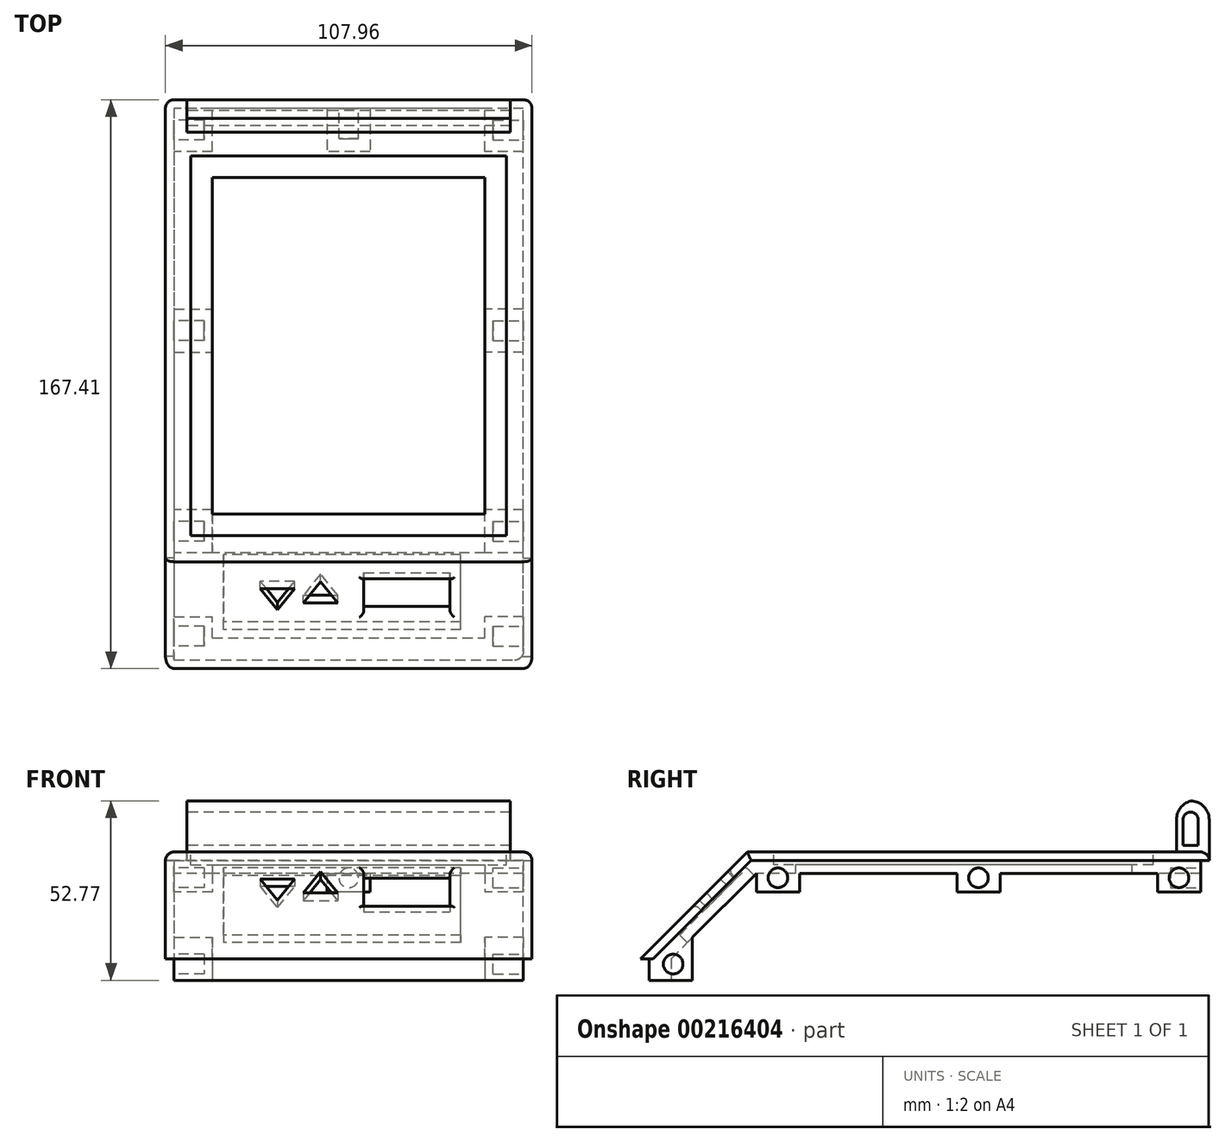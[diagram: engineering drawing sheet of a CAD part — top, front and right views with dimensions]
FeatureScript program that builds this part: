
annotation { "Feature Type Name" : "Feature", "Feature Type Description" : "" }
export const myFeature = defineFeature(function(context is Context, id is Id, definition is map)
    precondition{}
    {
        {
            var Q0;
            Q0=qCreatedBy(makeId("Top.planeOp"),FACE);
            var sketch = newSketch(context, id + "F0", { "sketchPlane" : qUnion([Q0])});
            skLineSegment(sketch, "E0.bottom", {"start": v(-40.13, 49.53) * mm, "end": v(40.13, 49.53) * mm});
            skLineSegment(sketch, "E0.top", {"start": v(-40.13, -49.53) * mm, "end": v(40.13, -49.53) * mm});
            skLineSegment(sketch, "E0.left", {"start": v(-40.13, 49.53) * mm, "end": v(-40.13, -49.53) * mm});
            skLineSegment(sketch, "E0.right", {"start": v(40.13, 49.53) * mm, "end": v(40.13, -49.53) * mm});
            skPoint(sketch, "E0.middle", {"position": v(0, 0) * mm});
            skLineSegment(sketch, "E1.bottom", {"start": v(53.97, -60.96) * mm, "end": v(-53.98, -60.96) * mm});
            skLineSegment(sketch, "E1.top", {"start": v(53.97, 72.4) * mm, "end": v(-53.98, 72.39) * mm});
            skLineSegment(sketch, "E1.left", {"start": v(53.98, -60.96) * mm, "end": v(53.98, 72.4) * mm});
            skLineSegment(sketch, "E1.right", {"start": v(-53.98, -60.96) * mm, "end": v(-53.98, 72.39) * mm});
            skSolve(sketch);
        }
        {
            var Q0;
            Q0 = qSketchRegion(id + "F0", true);
            extrude(context, id + "F1", {"entities" : qUnion([Q0]), "depth" : 6.35 * mm});
        }
        {
            var Q0;
            Q0=makeQuery(id+"F1.opExtrude","CAP_FACE",FACE,{"disambiguationData":[OSD([sQuery(id+"F0.wireOp",EDGE,"E0.bottom"),sQuery(id+"F0.wireOp",EDGE,"E0.top"),sQuery(id+"F0.wireOp",EDGE,"E0.left"),sQuery(id+"F0.wireOp",EDGE,"E0.right"),sQuery(id+"F0.wireOp",EDGE,"E1.bottom"),sQuery(id+"F0.wireOp",EDGE,"E1.top"),sQuery(id+"F0.wireOp",EDGE,"E1.left"),sQuery(id+"F0.wireOp",EDGE,"E1.right")])],"isStart":false});
            var sketch = newSketch(context, id + "F2", { "sketchPlane" : qUnion([Q0])});
            skPoint(sketch, "E2.middle", {"position": v(0, 0) * mm});
            skLineSegment(sketch, "E3.0", {"start": v(-46.48, 55.88) * mm, "end": v(46.48, 55.88) * mm});
            skLineSegment(sketch, "E3.1", {"start": v(-46.48, 55.88) * mm, "end": v(-46.48, -55.88) * mm});
            skLineSegment(sketch, "E3.2", {"start": v(-46.48, -55.88) * mm, "end": v(46.48, -55.88) * mm});
            skLineSegment(sketch, "E3.3", {"start": v(46.48, 55.88) * mm, "end": v(46.48, -55.88) * mm});
            skSolve(sketch);
        }
        {
            var Q0;
            Q0 = qSketchRegion(id + "F2", true);
            extrude(context, id + "F3", {"entities" : qUnion([Q0]), "operationType" : NewBodyOperationType.REMOVE, "oppositeDirection" : true, "depth" : 3.8 * mm});
        }
        {
            var Q0;
            Q0=makeQuery(id+"F1.opExtrude","SWEPT_FACE",FACE,{"disambiguationData":[OSD([sQuery(id+"F0.wireOp",EDGE,"E1.left")])]});
            var sketch = newSketch(context, id + "F4", { "sketchPlane" : qUnion([Q0])});
            skLineSegment(sketch, "E4", {"start": v(-60.96, 0) * mm, "end": v(-86.04, -25.08) * mm});
            skLineSegment(sketch, "E5", {"start": v(-95.02, -25.08) * mm, "end": v(-63.6, 6.35) * mm});
            skLineSegment(sketch, "E6", {"start": v(-63.6, 6.35) * mm, "end": v(-60.96, 6.35) * mm});
            skLineSegment(sketch, "E7", {"start": v(-60.96, 0) * mm, "end": v(-60.96, 6.35) * mm});
            skLineSegment(sketch, "E8", {"start": v(-95.02, -25.08) * mm, "end": v(-95.02, -31.43) * mm});
            skLineSegment(sketch, "E9", {"start": v(-86.04, -31.43) * mm, "end": v(-86.04, -25.08) * mm});
            skLineSegment(sketch, "E10", {"start": v(-86.04, -25.08) * mm, "end": v(-95.02, -25.08) * mm});
            skLineSegment(sketch, "E11", {"start": v(-95.02, -31.43) * mm, "end": v(-86.04, -31.43) * mm});
            skSolve(sketch);
        }
        {
            var Q0;
            Q0 = qSketchRegion(id + "F4", true);
            var Q1;
            Q1=makeQuery(id+"F1.opExtrude","SWEPT_FACE",FACE,{"disambiguationData":[OSD([sQuery(id+"F0.wireOp",EDGE,"E1.right")])]});
            extrude(context, id + "F5", {"entities" : qUnion([Q0]), "operationType" : NewBodyOperationType.ADD, "endBound" : BoundingType.UP_TO_SURFACE, "oppositeDirection" : true, "endBoundEntityFace" : qUnion([Q1]), "depth" : 101.6 * mm});
        }
        {
            var Q0;
            Q0=makeQuery(id+"F5.opExtrude","SWEPT_FACE",FACE,{"disambiguationData":[OSD([sQuery(id+"F4.wireOp",EDGE,"E8")])]});
            var sketch = newSketch(context, id + "F6", { "sketchPlane" : qUnion([Q0])});
            skLineSegment(sketch, "E12.bottom", {"start": v(53.98, -25.08) * mm, "end": v(-53.97, -25.08) * mm});
            skLineSegment(sketch, "E12.top", {"start": v(53.98, -31.43) * mm, "end": v(-53.97, -31.43) * mm});
            skLineSegment(sketch, "E12.left", {"start": v(53.98, -25.08) * mm, "end": v(53.98, -31.43) * mm});
            skLineSegment(sketch, "E12.right", {"start": v(-53.97, -25.08) * mm, "end": v(-53.97, -31.43) * mm});
            skSolve(sketch);
        }
        {
            var Q0;
            Q0 = qSketchRegion(id + "F6", true);
            extrude(context, id + "F7", {"entities" : qUnion([Q0]), "operationType" : NewBodyOperationType.REMOVE, "oppositeDirection" : true, "depth" : 2.54 * mm});
        }
        {
            var Q0;
            Q0=makeQuery(id+"F5.boolean.opBoolean","MERGE",FACE,{"derivedFrom":[makeQuery(id+"F1.opExtrude","SWEPT_FACE",FACE,{"disambiguationData":[OSD([sQuery(id+"F0.wireOp",EDGE,"E1.left")])]}),makeQuery(id+"F5.opExtrude","CAP_FACE",FACE,{"disambiguationData":[OSD([sQuery(id+"F4.wireOp",EDGE,"E4"),sQuery(id+"F4.wireOp",EDGE,"E5"),sQuery(id+"F4.wireOp",EDGE,"E6"),sQuery(id+"F4.wireOp",EDGE,"E7"),sQuery(id+"F4.wireOp",EDGE,"E8"),sQuery(id+"F4.wireOp",EDGE,"E9"),sQuery(id+"F4.wireOp",EDGE,"E11")])],"isStart":true})]});
            var sketch = newSketch(context, id + "F8", { "sketchPlane" : qUnion([Q0])});
            skLineSegment(sketch, "E13.0", {"start": v(-62.54, 3.81) * mm, "end": v(72.4, 3.81) * mm});
            skLineSegment(sketch, "E13.1", {"start": v(-103.18, -36.83) * mm, "end": v(-62.54, 3.81) * mm});
            skLineSegment(sketch, "E14", {"start": v(72.4, 3.81) * mm, "end": v(72.4, -36.83) * mm});
            skLineSegment(sketch, "E15", {"start": v(72.4, -36.83) * mm, "end": v(-103.18, -36.83) * mm});
            skLineSegment(sketch, "E16", {"start": v(-92.48, -25.08) * mm, "end": v(-91.43, -25.08) * mm});
            skLineSegment(sketch, "E17", {"start": v(-91.43, -25.08) * mm, "end": v(-92.48, -26.13) * mm});
            skLineSegment(sketch, "E18", {"start": v(-92.48, -26.13) * mm, "end": v(-92.48, -25.08) * mm});
            skSolve(sketch);
        }
        {
            var Q0;
            Q0 = qSketchRegion(id + "F8", true);
            extrude(context, id + "F9", {"entities" : qUnion([Q0]), "operationType" : NewBodyOperationType.REMOVE, "oppositeDirection" : true, "depth" : 2.54 * mm});
        }
        {
            var Q0;
            Q0=makeQuery(id+"F1.opExtrude","SWEPT_FACE",FACE,{"disambiguationData":[OSD([sQuery(id+"F0.wireOp",EDGE,"E1.top")])]});
            var sketch = newSketch(context, id + "F10", { "sketchPlane" : qUnion([Q0])});
            skLineSegment(sketch, "E19.bottom", {"start": v(-51.43, 3.81) * mm, "end": v(53.98, 3.81) * mm});
            skLineSegment(sketch, "E19.top", {"start": v(-51.43, 0) * mm, "end": v(53.98, 0) * mm});
            skLineSegment(sketch, "E19.left", {"start": v(-51.43, 3.81) * mm, "end": v(-51.43, 0) * mm});
            skLineSegment(sketch, "E19.right", {"start": v(53.98, 3.81) * mm, "end": v(53.98, 0) * mm});
            skSolve(sketch);
        }
        {
            var Q0;
            Q0 = qSketchRegion(id + "F10", true);
            extrude(context, id + "F11", {"entities" : qUnion([Q0]), "operationType" : NewBodyOperationType.REMOVE, "oppositeDirection" : true, "depth" : 2.54 * mm});
        }
        {
            var Q0;
            Q0=makeQuery(id+"F5.boolean.opBoolean","MERGE",FACE,{"derivedFrom":[makeQuery(id+"F1.opExtrude","SWEPT_FACE",FACE,{"disambiguationData":[OSD([sQuery(id+"F0.wireOp",EDGE,"E1.right")])]}),makeQuery(id+"F5.opExtrude","CAP_FACE",FACE,{"disambiguationData":[OSD([sQuery(id+"F4.wireOp",EDGE,"E4"),sQuery(id+"F4.wireOp",EDGE,"E5"),sQuery(id+"F4.wireOp",EDGE,"E6"),sQuery(id+"F4.wireOp",EDGE,"E7"),sQuery(id+"F4.wireOp",EDGE,"E8"),sQuery(id+"F4.wireOp",EDGE,"E9"),sQuery(id+"F4.wireOp",EDGE,"E11")])],"isStart":false})]});
            var sketch = newSketch(context, id + "F12", { "sketchPlane" : qUnion([Q0])});
            skLineSegment(sketch, "E20", {"start": v(-69.85, 3.81) * mm, "end": v(62.54, 3.81) * mm});
            skLineSegment(sketch, "E21", {"start": v(62.54, 3.81) * mm, "end": v(91.43, -25.08) * mm});
            skLineSegment(sketch, "E22", {"start": v(91.43, -25.08) * mm, "end": v(92.48, -25.08) * mm});
            skLineSegment(sketch, "E23", {"start": v(92.48, -25.08) * mm, "end": v(92.48, -36.69) * mm});
            skLineSegment(sketch, "E24", {"start": v(92.48, -36.69) * mm, "end": v(-69.85, -36.69) * mm});
            skLineSegment(sketch, "E25", {"start": v(-69.85, -36.69) * mm, "end": v(-69.85, 3.81) * mm});
            skLineSegment(sketch, "E26", {"start": v(92.48, -25.08) * mm, "end": v(91.43, -25.08) * mm});
            skSolve(sketch);
        }
        {
            var Q0;
            Q0 = qSketchRegion(id + "F12", true);
            extrude(context, id + "F13", {"entities" : qUnion([Q0]), "operationType" : NewBodyOperationType.REMOVE, "oppositeDirection" : true, "depth" : 2.54 * mm});
        }
        {
            var Q0;
            Q0=qCreatedBy(makeId("Right.planeOp"),FACE);
            var sketch = newSketch(context, id + "F14", { "sketchPlane" : qUnion([Q0])});
            skLineSegment(sketch, "E27.top", {"start": v(61.47, 6.35) * mm, "end": v(72.4, 6.35) * mm});
            skLineSegment(sketch, "E27.left", {"start": v(61.47, 15.88) * mm, "end": v(61.47, 6.35) * mm});
            skLineSegment(sketch, "E27.right", {"start": v(72.4, 15.88) * mm, "end": v(72.4, 6.35) * mm});
            skLineSegment(sketch, "E28", {"start": v(66.93, 15.88) * mm, "end": v(66.93, 8.26) * mm});
            skLineSegment(sketch, "E29.0.left", {"start": v(69.15, 15.88) * mm, "end": v(69.15, 8.26) * mm});
            skLineSegment(sketch, "E29.0.right", {"start": v(64.7, 15.88) * mm, "end": v(64.7, 8.26) * mm});
            skArc(sketch, "E30", {"start": v(69.15, 15.88) * mm, "mid": v(66.93, 18.1) * mm, "end": v(64.7, 15.88) * mm});
            skArc(sketch, "E31", {"start": v(72.4, 15.88) * mm, "mid": v(66.93, 21.34) * mm, "end": v(61.47, 15.88) * mm});
            skLineSegment(sketch, "E32", {"start": v(64.7, 8.26) * mm, "end": v(69.15, 8.26) * mm});
            skLineSegment(sketch, "E33", {"start": v(62.8, 6.35) * mm, "end": v(62.8, 15.94) * mm});
            skArc(sketch, "E34", {"start": v(66.93, 21.34) * mm, "mid": v(63.95, 19.34) * mm, "end": v(62.8, 15.94) * mm});
            skSolve(sketch);
        }
        {
            var Q0;
            Q0=makeQuery(id+"F5.boolean.opBoolean","MERGE",EDGE,{"derivedFrom":[makeQuery(id+"F1.opExtrude","CAP_EDGE",EDGE,{"disambiguationData":[OSD([sQuery(id+"F0.wireOp",EDGE,"E1.left")])],"isStart":false}),makeQuery(id+"F5.opExtrude","CAP_EDGE",EDGE,{"disambiguationData":[OSD([sQuery(id+"F4.wireOp",EDGE,"E6")])],"isStart":true})]});
            var Q1;
            Q1=makeQuery(id+"F5.opExtrude","CAP_EDGE",EDGE,{"disambiguationData":[OSD([sQuery(id+"F4.wireOp",EDGE,"E5")])],"isStart":true});
            var Q2;
            Q2=makeQuery(id+"F5.boolean.opBoolean","MERGE",EDGE,{"derivedFrom":[makeQuery(id+"F1.opExtrude","CAP_EDGE",EDGE,{"disambiguationData":[OSD([sQuery(id+"F0.wireOp",EDGE,"E1.right")])],"isStart":false}),makeQuery(id+"F5.opExtrude","CAP_EDGE",EDGE,{"disambiguationData":[OSD([sQuery(id+"F4.wireOp",EDGE,"E6")])],"isStart":false})]});
            var Q3;
            Q3=makeQuery(id+"F5.opExtrude","CAP_EDGE",EDGE,{"disambiguationData":[OSD([sQuery(id+"F4.wireOp",EDGE,"E5")])],"isStart":false});
            fillet(context, id + "F15", {"entities" : qUnion([Q0, Q1, Q2, Q3]), "radius" : 2.54 * mm, "tangentPropagation" : true, "allowEdgeOverflow" : false});
        }
        {
            var Q0;
            {var subQ2=sQuery(id+"F14.wireOp",EDGE,"E27.right");Q0=makeQuery(id+"F14.imprint","IMPRINT",FACE,{"disambiguationData":[TD([[makeQuery(id+"F14.imprint","IMPRINT",EDGE,{"derivedFrom":subQ2}),-1.0]])]});}
            extrude(context, id + "F16", {"entities" : qUnion([Q0]), "operationType" : NewBodyOperationType.ADD, "endBound" : BoundingType.SYMMETRIC, "depth" : 95.25 * mm});
        }
        {
            var Q0;
            Q0=makeQuery(id+"F5.opExtrude","SWEPT_FACE",FACE,{"disambiguationData":[OSD([sQuery(id+"F4.wireOp",EDGE,"E4")])]});
            var sketch = newSketch(context, id + "F17", { "sketchPlane" : qUnion([Q0])});
            skLineSegment(sketch, "E35.bottom", {"start": v(-29.85, -62.28) * mm, "end": v(-4.45, -62.28) * mm});
            skLineSegment(sketch, "E35.top", {"start": v(-29.85, -48.31) * mm, "end": v(-4.45, -48.31) * mm});
            skLineSegment(sketch, "E35.left", {"start": v(-29.85, -62.28) * mm, "end": v(-29.85, -48.31) * mm});
            skLineSegment(sketch, "E35.right", {"start": v(-4.45, -62.28) * mm, "end": v(-4.45, -48.31) * mm});
            skSolve(sketch);
        }
        {
            var Q0;
            Q0 = qSketchRegion(id + "F17", true);
            extrude(context, id + "F18", {"entities" : qUnion([Q0]), "operationType" : NewBodyOperationType.REMOVE, "oppositeDirection" : true, "depth" : 25.4 * mm});
        }
        {
            var Q0;
            Q0=makeQuery(id+"F5.opExtrude","SWEPT_FACE",FACE,{"disambiguationData":[OSD([sQuery(id+"F4.wireOp",EDGE,"E4")])]});
            var sketch = newSketch(context, id + "F19", { "sketchPlane" : qUnion([Q0])});
            skLineSegment(sketch, "E36.bottom", {"start": v(-33.02, -71.86) * mm, "end": v(-1.27, -71.86) * mm});
            skLineSegment(sketch, "E36.top", {"start": v(-33.02, -43.92) * mm, "end": v(-1.27, -43.92) * mm});
            skLineSegment(sketch, "E36.left", {"start": v(-33.02, -71.86) * mm, "end": v(-33.02, -43.92) * mm});
            skLineSegment(sketch, "E36.right", {"start": v(-1.27, -71.86) * mm, "end": v(-1.27, -43.92) * mm});
            skLineSegment(sketch, "E37", {"start": v(-17.15, -48.31) * mm, "end": v(-17.15, -43.92) * mm});
            skSolve(sketch);
        }
        {
            var Q0;
            Q0 = qSketchRegion(id + "F19", true);
            extrude(context, id + "F20", {"entities" : qUnion([Q0]), "operationType" : NewBodyOperationType.REMOVE, "oppositeDirection" : true, "depth" : 3.17 * mm});
        }
        {
            var Q0;
            Q0=makeQuery(id+"F5.opExtrude","SWEPT_FACE",FACE,{"disambiguationData":[OSD([sQuery(id+"F4.wireOp",EDGE,"E4")])]});
            var sketch = newSketch(context, id + "F21", { "sketchPlane" : qUnion([Q0])});
            skLineSegment(sketch, "E38.bottom", {"start": v(-1.27, -43.92) * mm, "end": v(36.83, -43.92) * mm});
            skLineSegment(sketch, "E38.top", {"start": v(-1.27, -71.86) * mm, "end": v(36.83, -71.86) * mm});
            skLineSegment(sketch, "E38.left", {"start": v(-1.27, -43.92) * mm, "end": v(-1.27, -71.86) * mm});
            skLineSegment(sketch, "E38.right", {"start": v(36.83, -43.92) * mm, "end": v(36.83, -71.86) * mm});
            skSolve(sketch);
        }
        {
            var Q0;
            Q0 = qSketchRegion(id + "F21", true);
            var Q1;
            Q1=makeQuery(id+"F20.boolean.opBoolean","COPY",FACE,{"derivedFrom":makeQuery(id+"F20.opExtrude","CAP_FACE",FACE,{"disambiguationData":[OSD([sQuery(id+"F19.wireOp",EDGE,"E36.bottom"),sQuery(id+"F19.wireOp",EDGE,"E36.top"),sQuery(id+"F19.wireOp",EDGE,"E36.left"),sQuery(id+"F19.wireOp",EDGE,"E36.right")])],"isStart":false})});
            extrude(context, id + "F22", {"entities" : qUnion([Q0]), "operationType" : NewBodyOperationType.REMOVE, "endBound" : BoundingType.UP_TO_SURFACE, "oppositeDirection" : true, "endBoundEntityFace" : qUnion([Q1]), "depth" : 25.4 * mm});
        }
        {
            var Q0;
            Q0=makeQuery(id+"F22.boolean.opBoolean","MERGE",FACE,{"derivedFrom":[makeQuery(id+"F20.boolean.opBoolean","COPY",FACE,{"derivedFrom":makeQuery(id+"F20.opExtrude","CAP_FACE",FACE,{"disambiguationData":[OSD([sQuery(id+"F19.wireOp",EDGE,"E36.bottom"),sQuery(id+"F19.wireOp",EDGE,"E36.top"),sQuery(id+"F19.wireOp",EDGE,"E36.left"),sQuery(id+"F19.wireOp",EDGE,"E36.right")])],"isStart":false})})],"fromTools":[makeQuery(id+"F22.opExtrude","CAP_FACE",FACE,{"disambiguationData":[OSD([sQuery(id+"F21.wireOp",EDGE,"E38.bottom"),sQuery(id+"F21.wireOp",EDGE,"E38.top"),sQuery(id+"F21.wireOp",EDGE,"E38.left"),sQuery(id+"F21.wireOp",EDGE,"E38.right")])],"isStart":false})]});
            var sketch = newSketch(context, id + "F23", { "sketchPlane" : qUnion([Q0])});
            skLineSegment(sketch, "E39", {"start": v(-4.45, -54.66) * mm, "end": v(20.95, -54.66) * mm});
            skCircle(sketch, "E40.cCircle", {"center": v(8.25, -54.66) * mm, "radius": 2.93 * mm, "construction": true});
            skLineSegment(sketch, "E40.0", {"start": v(8.25, -48.8) * mm, "end": v(13.33, -57.6) * mm});
            skLineSegment(sketch, "E40.1", {"start": v(13.33, -57.6) * mm, "end": v(3.17, -57.6) * mm});
            skLineSegment(sketch, "E40.2", {"start": v(3.17, -57.6) * mm, "end": v(8.25, -48.8) * mm});
            skPoint(sketch, "E40.0.midPoint", {"position": v(10.8, -53.2) * mm});
            skCircle(sketch, "E41.cCircle", {"center": v(20.95, -54.66) * mm, "radius": 2.93 * mm, "construction": true});
            skPoint(sketch, "E41.cCircle.perimeterSnap0", {"position": v(5.71, -53.2) * mm});
            skLineSegment(sketch, "E41.0", {"start": v(15.87, -51.73) * mm, "end": v(26.03, -51.73) * mm});
            skLineSegment(sketch, "E41.1", {"start": v(26.03, -51.73) * mm, "end": v(20.95, -60.53) * mm});
            skLineSegment(sketch, "E41.2", {"start": v(20.95, -60.53) * mm, "end": v(15.87, -51.73) * mm});
            skPoint(sketch, "E41.0.midPoint", {"position": v(20.95, -51.73) * mm});
            skPoint(sketch, "E41.0.midPoint.positionSnap0", {"position": v(5.71, -53.2) * mm});
            skSolve(sketch);
        }
        {
            var Q0;
            Q0 = qSketchRegion(id + "F23", true);
            extrude(context, id + "F24", {"entities" : qUnion([Q0]), "operationType" : NewBodyOperationType.REMOVE, "oppositeDirection" : true, "depth" : 25.4 * mm});
        }
        {
            var Q0;
            {var subQ0=sQuery(id+"F4.wireOp",EDGE,"E6");var subQ1=sQuery(id+"F0.wireOp",EDGE,"E1.left");var subQ3=sQuery(id+"F0.wireOp",EDGE,"E1.top");Q0=makeQuery(id+"F16.boolean.opBoolean","SPLIT",EDGE,{"disambiguationData":[TD([makeQuery(id+"F15.opFillet","BLEND_FACE",FACE,{"disambiguationData":[OSD([subQ1,subQ0])]})])],"derivedFrom":makeQuery(id+"F1.opExtrude","CAP_EDGE",EDGE,{"disambiguationData":[OSD([subQ3])],"isStart":false})});}
            var Q1;
            {var subQ0=sQuery(id+"F4.wireOp",EDGE,"E6");var subQ1=sQuery(id+"F0.wireOp",EDGE,"E1.right");var subQ3=sQuery(id+"F0.wireOp",EDGE,"E1.top");Q1=makeQuery(id+"F16.boolean.opBoolean","SPLIT",EDGE,{"disambiguationData":[TD([makeQuery(id+"F15.opFillet","BLEND_FACE",FACE,{"disambiguationData":[OSD([subQ1,subQ0])]})])],"derivedFrom":makeQuery(id+"F1.opExtrude","CAP_EDGE",EDGE,{"disambiguationData":[OSD([subQ3])],"isStart":false})});}
            fillet(context, id + "F25", {"entities" : qUnion([Q0, Q1]), "radius" : 2.54 * mm, "tangentPropagation" : true, "allowEdgeOverflow" : false});
        }
        {
            var Q0;
            Q0=makeQuery(id+"F18.boolean.opBoolean","INTERSECT",EDGE,{"derivedFrom":[makeQuery(id+"F5.opExtrude","SWEPT_FACE",FACE,{"disambiguationData":[OSD([sQuery(id+"F4.wireOp",EDGE,"E5")])]}),makeQuery(id+"F18.opExtrude","SWEPT_FACE",FACE,{"disambiguationData":[OSD([sQuery(id+"F17.wireOp",EDGE,"E35.right")])]})]});
            var Q1;
            Q1=makeQuery(id+"F18.boolean.opBoolean","INTERSECT",EDGE,{"derivedFrom":[makeQuery(id+"F5.opExtrude","SWEPT_FACE",FACE,{"disambiguationData":[OSD([sQuery(id+"F4.wireOp",EDGE,"E5")])]}),makeQuery(id+"F18.opExtrude","SWEPT_FACE",FACE,{"disambiguationData":[OSD([sQuery(id+"F17.wireOp",EDGE,"E35.left")])]})]});
            var Q2;
            Q2=makeQuery(id+"F18.boolean.opBoolean","INTERSECT",EDGE,{"derivedFrom":[makeQuery(id+"F5.opExtrude","SWEPT_FACE",FACE,{"disambiguationData":[OSD([sQuery(id+"F4.wireOp",EDGE,"E5")])]}),makeQuery(id+"F18.opExtrude","SWEPT_FACE",FACE,{"disambiguationData":[OSD([sQuery(id+"F17.wireOp",EDGE,"E35.bottom")])]})]});
            var Q3;
            Q3=makeQuery(id+"F18.boolean.opBoolean","INTERSECT",EDGE,{"derivedFrom":[makeQuery(id+"F5.opExtrude","SWEPT_FACE",FACE,{"disambiguationData":[OSD([sQuery(id+"F4.wireOp",EDGE,"E5")])]}),makeQuery(id+"F18.opExtrude","SWEPT_FACE",FACE,{"disambiguationData":[OSD([sQuery(id+"F17.wireOp",EDGE,"E35.top")])]})]});
            fillet(context, id + "F26", {"entities" : qUnion([Q0, Q1, Q2, Q3]), "radius" : 1.27 * mm, "tangentPropagation" : true, "allowEdgeOverflow" : false});
        }
        {
            var Q0;
            Q0=makeQuery(id+"F5.opExtrude","SWEPT_FACE",FACE,{"disambiguationData":[OSD([sQuery(id+"F4.wireOp",EDGE,"E11")])]});
            var sketch = newSketch(context, id + "F27", { "sketchPlane" : qUnion([Q0])});
            skLineSegment(sketch, "E42.bottom", {"start": v(-40.13, -10.8) * mm, "end": v(-51.44, -10.8) * mm});
            skLineSegment(sketch, "E42.top", {"start": v(-40.13, 1.9) * mm, "end": v(-51.44, 1.9) * mm});
            skLineSegment(sketch, "E42.left", {"start": v(-40.13, -10.8) * mm, "end": v(-40.13, 1.9) * mm});
            skLineSegment(sketch, "E42.right", {"start": v(-51.44, -10.8) * mm, "end": v(-51.44, 1.9) * mm});
            skLineSegment(sketch, "E43.bottom", {"start": v(40.13, -10.8) * mm, "end": v(51.44, -10.8) * mm});
            skLineSegment(sketch, "E43.top", {"start": v(40.13, 1.9) * mm, "end": v(51.44, 1.9) * mm});
            skLineSegment(sketch, "E43.left", {"start": v(40.13, -10.8) * mm, "end": v(40.13, 1.9) * mm});
            skLineSegment(sketch, "E43.right", {"start": v(51.44, -10.8) * mm, "end": v(51.44, 1.9) * mm});
            skLineSegment(sketch, "E44.bottom", {"start": v(-51.44, 92.48) * mm, "end": v(-40.13, 92.48) * mm});
            skLineSegment(sketch, "E44.top", {"start": v(-51.44, 79.78) * mm, "end": v(-40.13, 79.78) * mm});
            skLineSegment(sketch, "E44.left", {"start": v(-51.44, 92.48) * mm, "end": v(-51.44, 79.78) * mm});
            skLineSegment(sketch, "E44.right", {"start": v(-40.13, 92.48) * mm, "end": v(-40.13, 79.78) * mm});
            skLineSegment(sketch, "E45.bottom", {"start": v(51.44, 92.48) * mm, "end": v(40.13, 92.48) * mm});
            skLineSegment(sketch, "E45.top", {"start": v(51.44, 79.78) * mm, "end": v(40.13, 79.78) * mm});
            skLineSegment(sketch, "E45.left", {"start": v(51.44, 92.48) * mm, "end": v(51.44, 79.78) * mm});
            skLineSegment(sketch, "E45.right", {"start": v(40.13, 92.48) * mm, "end": v(40.13, 79.78) * mm});
            skLineSegment(sketch, "E46.bottom", {"start": v(-51.44, -69.85) * mm, "end": v(-40.13, -69.85) * mm});
            skLineSegment(sketch, "E46.top", {"start": v(-51.44, -57.15) * mm, "end": v(-40.13, -57.15) * mm});
            skLineSegment(sketch, "E46.left", {"start": v(-51.44, -69.85) * mm, "end": v(-51.44, -57.15) * mm});
            skLineSegment(sketch, "E46.right", {"start": v(-40.13, -69.85) * mm, "end": v(-40.13, -57.15) * mm});
            skLineSegment(sketch, "E47.bottom", {"start": v(40.13, -69.85) * mm, "end": v(51.44, -69.85) * mm});
            skLineSegment(sketch, "E47.top", {"start": v(40.13, -57.15) * mm, "end": v(51.44, -57.15) * mm});
            skLineSegment(sketch, "E47.left", {"start": v(40.13, -69.85) * mm, "end": v(40.13, -57.15) * mm});
            skLineSegment(sketch, "E47.right", {"start": v(51.44, -69.85) * mm, "end": v(51.44, -57.15) * mm});
            skLineSegment(sketch, "E48.bottom", {"start": v(-51.44, 48.26) * mm, "end": v(-40.13, 48.26) * mm});
            skLineSegment(sketch, "E48.top", {"start": v(-51.44, 60.96) * mm, "end": v(-40.13, 60.96) * mm});
            skLineSegment(sketch, "E48.left", {"start": v(-51.44, 48.26) * mm, "end": v(-51.44, 60.96) * mm});
            skLineSegment(sketch, "E48.right", {"start": v(-40.13, 48.26) * mm, "end": v(-40.13, 60.96) * mm});
            skLineSegment(sketch, "E49.bottom", {"start": v(40.13, 60.96) * mm, "end": v(51.44, 60.96) * mm});
            skLineSegment(sketch, "E49.top", {"start": v(40.13, 48.26) * mm, "end": v(51.44, 48.26) * mm});
            skLineSegment(sketch, "E49.left", {"start": v(40.13, 60.96) * mm, "end": v(40.13, 48.26) * mm});
            skLineSegment(sketch, "E49.right", {"start": v(51.44, 60.96) * mm, "end": v(51.44, 48.26) * mm});
            skLineSegment(sketch, "E50.bottom", {"start": v(-6.35, -57.15) * mm, "end": v(6.35, -57.15) * mm});
            skLineSegment(sketch, "E50.top", {"start": v(-6.35, -69.85) * mm, "end": v(6.35, -69.85) * mm});
            skLineSegment(sketch, "E50.left", {"start": v(-6.35, -57.15) * mm, "end": v(-6.35, -69.85) * mm});
            skLineSegment(sketch, "E50.right", {"start": v(6.35, -57.15) * mm, "end": v(6.35, -69.85) * mm});
            skPoint(sketch, "E51", {"position": v(0, -57.15) * mm});
            skPoint(sketch, "E52", {"position": v(-40.13, -4.45) * mm});
            skPoint(sketch, "E53", {"position": v(40.13, -4.45) * mm});
            skSolve(sketch);
        }
        {
            var Q0;
            Q0=makeQuery(id+"F27.imprint","IMPRINT",FACE,{"disambiguationData":[TD([[makeQuery(id+"F27.imprint","IMPRINT",EDGE,{"derivedFrom":sQuery(id+"F27.wireOp",EDGE,"oBJHuU9w-AG7v-fE7F-7dsP-lNij15PUJmbG.bottom")}),1.0]])]});
            var Q1;
            Q1=makeQuery(id+"F27.imprint","IMPRINT",FACE,{"disambiguationData":[TD([[makeQuery(id+"F27.imprint","IMPRINT",EDGE,{"derivedFrom":sQuery(id+"F27.wireOp",EDGE,"E43.bottom")}),1.0]])]});
            var Q2;
            {var subQ0=sQuery(id+"F27.wireOp",EDGE,"E45.top");Q2=makeQuery(id+"F27.imprint","IMPRINT",FACE,{"disambiguationData":[TD([[makeQuery(id+"F27.imprint","IMPRINT",EDGE,{"derivedFrom":subQ0}),-1.0]])]});}
            var Q3;
            {var subQ0=sQuery(id+"F27.wireOp",EDGE,"E44.top");Q3=makeQuery(id+"F27.imprint","IMPRINT",FACE,{"disambiguationData":[TD([[makeQuery(id+"F27.imprint","IMPRINT",EDGE,{"derivedFrom":subQ0}),1.0]])]});}
            var Q4;
            Q4=makeQuery(id+"F27.imprint","IMPRINT",FACE,{"disambiguationData":[TD([[makeQuery(id+"F27.imprint","IMPRINT",EDGE,{"derivedFrom":sQuery(id+"F27.wireOp",EDGE,"E42.bottom")}),-1.0]])]});
            var Q5;
            Q5=makeQuery(id+"F27.imprint","IMPRINT",FACE,{"disambiguationData":[TD([[makeQuery(id+"F27.imprint","IMPRINT",EDGE,{"derivedFrom":sQuery(id+"F27.wireOp",EDGE,"E46.bottom")}),1.0]])]});
            var Q6;
            Q6=makeQuery(id+"F27.imprint","IMPRINT",FACE,{"disambiguationData":[TD([[makeQuery(id+"F27.imprint","IMPRINT",EDGE,{"derivedFrom":sQuery(id+"F27.wireOp",EDGE,"E47.bottom")}),1.0]])]});
            var Q7;
            Q7=makeQuery(id+"F27.imprint","IMPRINT",FACE,{"disambiguationData":[TD([[makeQuery(id+"F27.imprint","IMPRINT",EDGE,{"derivedFrom":sQuery(id+"F27.wireOp",EDGE,"E48.bottom")}),1.0]])]});
            var Q8;
            Q8=makeQuery(id+"F27.imprint","IMPRINT",FACE,{"disambiguationData":[TD([[makeQuery(id+"F27.imprint","IMPRINT",EDGE,{"derivedFrom":sQuery(id+"F27.wireOp",EDGE,"E49.bottom")}),-1.0]])]});
            var Q9;
            Q9=makeQuery(id+"F27.imprint","IMPRINT",FACE,{"disambiguationData":[TD([[makeQuery(id+"F27.imprint","IMPRINT",EDGE,{"derivedFrom":sQuery(id+"F27.wireOp",EDGE,"E50.bottom")}),-1.0]])]});
            var Q10;
            Q10=makeQuery(id+"F1.opExtrude","SWEPT_BODY",BODY,{"disambiguationData":[OSD([sQuery(id+"F0.wireOp",EDGE,"E0.bottom"),sQuery(id+"F0.wireOp",EDGE,"E0.top"),sQuery(id+"F0.wireOp",EDGE,"E0.left"),sQuery(id+"F0.wireOp",EDGE,"E0.right"),sQuery(id+"F0.wireOp",EDGE,"E1.bottom"),sQuery(id+"F0.wireOp",EDGE,"E1.top"),sQuery(id+"F0.wireOp",EDGE,"E1.left"),sQuery(id+"F0.wireOp",EDGE,"E1.right")])]});
            extrude(context, id + "F28", {"entities" : qUnion([Q0, Q1, Q2, Q3, Q4, Q5, Q6, Q7, Q8, Q9]), "operationType" : NewBodyOperationType.ADD, "endBound" : BoundingType.UP_TO_BODY, "oppositeDirection" : true, "endBoundEntityBody" : qUnion([Q10]), "depth" : 25.4 * mm});
        }
        {
            var Q0;
            Q0=makeQuery(id+"F28.boolean.opBoolean","MERGE",FACE,{"derivedFrom":[makeQuery(id+"F13.boolean.opBoolean","COPY",FACE,{"derivedFrom":makeQuery(id+"F13.opExtrude","CAP_FACE",FACE,{"disambiguationData":[OSD([sQuery(id+"F12.wireOp",EDGE,"E20"),sQuery(id+"F12.wireOp",EDGE,"E21"),sQuery(id+"F12.wireOp",EDGE,"E23"),sQuery(id+"F12.wireOp",EDGE,"E24"),sQuery(id+"F12.wireOp",EDGE,"E25"),sQuery(id+"F12.wireOp",EDGE,"E26")])],"isStart":false})}),makeQuery(id+"F28.opExtrude","SWEPT_FACE",FACE,{"disambiguationData":[OSD([sQuery(id+"F27.wireOp",EDGE,"E42.right")])]}),makeQuery(id+"F28.opExtrude","SWEPT_FACE",FACE,{"disambiguationData":[OSD([sQuery(id+"F27.wireOp",EDGE,"E44.left")])]}),makeQuery(id+"F28.opExtrude","SWEPT_FACE",FACE,{"disambiguationData":[OSD([sQuery(id+"F27.wireOp",EDGE,"E46.left")])]}),makeQuery(id+"F28.opExtrude","SWEPT_FACE",FACE,{"disambiguationData":[OSD([sQuery(id+"F27.wireOp",EDGE,"E48.left")])]})]});
            var sketch = newSketch(context, id + "F29", { "sketchPlane" : qUnion([Q0])});
            skLineSegment(sketch, "E54.bottom", {"start": v(-69.85, -5.46) * mm, "end": v(66.42, -5.46) * mm});
            skLineSegment(sketch, "E54.top", {"start": v(-69.85, -58.84) * mm, "end": v(70.65, -58.84) * mm});
            skLineSegment(sketch, "E54.left", {"start": v(-69.85, -5.46) * mm, "end": v(-69.85, -58.84) * mm});
            skLineSegment(sketch, "E54.right", {"start": v(70.65, -9.7) * mm, "end": v(70.65, -58.84) * mm});
            skLineSegment(sketch, "E55", {"start": v(63.5, -2.54) * mm, "end": v(79.78, -18.82) * mm});
            skLineSegment(sketch, "E56", {"start": v(79.78, -18.82) * mm, "end": v(79.78, -58.84) * mm});
            skLineSegment(sketch, "E57", {"start": v(79.78, -58.84) * mm, "end": v(70.65, -58.84) * mm});
            skPoint(sketch, "E58.start.orphan", {"position": v(96.06, -35.1) * mm});
            skLineSegment(sketch, "E59", {"start": v(63.5, -2.54) * mm, "end": v(-69.85, -2.54) * mm});
            skSolve(sketch);
        }
        {
            var Q0;
            Q0 = qSketchRegion(id + "F29", true);
            var Q1;
            {var subQ0=sQuery(id+"F29.wireOp",EDGE,"E55");var subQ1=sQuery(id+"F29.wireOp",EDGE,"E54.bottom");var subQ2=makeQuery(id+"F29.imprint","INTERSECT",VERTEX,{"derivedFrom":[subQ1,subQ0]});Q1=makeQuery(id+"F29.imprint","IMPRINT",FACE,{"disambiguationData":[TD([[makeQuery(id+"F29.imprint","IMPRINT",EDGE,{"disambiguationData":[TD([[subQ2,1.0]])],"derivedFrom":subQ1}),1.0]])]});}
            extrude(context, id + "F30", {"entities" : qUnion([Q0, Q1]), "operationType" : NewBodyOperationType.REMOVE, "oppositeDirection" : true, "depth" : 130.56 * mm});
        }
        {
            var Q0;
            {var subQ0=sQuery(id+"F12.wireOp",EDGE,"E25");Q0=makeQuery(id+"F28.boolean.opBoolean","MERGE",EDGE,{"derivedFrom":[makeQuery(id+"F13.boolean.opBoolean","COPY",EDGE,{"derivedFrom":makeQuery(id+"F13.opExtrude","CAP_EDGE",EDGE,{"disambiguationData":[OSD([subQ0])],"isStart":false})}),makeQuery(id+"F28.opExtrude","SWEPT_EDGE",EDGE,{"disambiguationData":[OSD([sQuery(id+"F0.wireOp",EDGE,"E0.bottom"),sQuery(id+"F0.wireOp",EDGE,"E0.top"),sQuery(id+"F0.wireOp",EDGE,"E0.left"),sQuery(id+"F0.wireOp",EDGE,"E0.right"),sQuery(id+"F0.wireOp",EDGE,"E1.bottom"),sQuery(id+"F0.wireOp",EDGE,"E1.top"),sQuery(id+"F0.wireOp",EDGE,"E1.left"),sQuery(id+"F0.wireOp",EDGE,"E1.right"),sQuery(id+"F12.wireOp",EDGE,"E20"),sQuery(id+"F12.wireOp",EDGE,"E21"),sQuery(id+"F12.wireOp",EDGE,"E23"),sQuery(id+"F12.wireOp",EDGE,"E24"),subQ0,sQuery(id+"F12.wireOp",EDGE,"E26")])]})]});}
            var Q1;
            {var subQ0=sQuery(id+"F10.wireOp",EDGE,"E19.left");Q1=makeQuery(id+"F28.boolean.opBoolean","MERGE",EDGE,{"derivedFrom":[makeQuery(id+"F11.boolean.opBoolean","COPY",EDGE,{"derivedFrom":makeQuery(id+"F11.opExtrude","CAP_EDGE",EDGE,{"disambiguationData":[OSD([subQ0])],"isStart":false})}),makeQuery(id+"F28.opExtrude","SWEPT_EDGE",EDGE,{"disambiguationData":[OSD([sQuery(id+"F10.wireOp",EDGE,"E19.top"),subQ0])]})]});}
            var Q2;
            Q2=makeQuery(id+"F13.boolean.opBoolean","COPY",EDGE,{"derivedFrom":makeQuery(id+"F13.opExtrude","CAP_EDGE",EDGE,{"disambiguationData":[OSD([sQuery(id+"F12.wireOp",EDGE,"E23")])],"isStart":false})});
            var Q3;
            Q3=makeQuery(id+"F9.boolean.opBoolean","INTERSECT",EDGE,{"derivedFrom":[makeQuery(id+"F7.boolean.opBoolean","COPY",FACE,{"derivedFrom":makeQuery(id+"F7.opExtrude","CAP_FACE",FACE,{"disambiguationData":[OSD([sQuery(id+"F6.wireOp",EDGE,"E12.bottom"),sQuery(id+"F6.wireOp",EDGE,"E12.top"),sQuery(id+"F6.wireOp",EDGE,"E12.left"),sQuery(id+"F6.wireOp",EDGE,"E12.right")])],"isStart":false})}),makeQuery(id+"F9.opExtrude","CAP_FACE",FACE,{"disambiguationData":[OSD([sQuery(id+"F8.wireOp",EDGE,"E13.0"),sQuery(id+"F8.wireOp",EDGE,"E13.1"),sQuery(id+"F8.wireOp",EDGE,"E14"),sQuery(id+"F8.wireOp",EDGE,"E15"),sQuery(id+"F8.wireOp",EDGE,"E16"),sQuery(id+"F8.wireOp",EDGE,"E18")])],"isStart":false})]});
            fillet(context, id + "F31", {"entities" : qUnion([Q0, Q1, Q2, Q3]), "radius" : 2.54 * mm, "allowEdgeOverflow" : false});
        }
        {
            var Q0;
            Q0=makeQuery(id+"F28.boolean.opBoolean","MERGE",FACE,{"derivedFrom":[makeQuery(id+"F9.boolean.opBoolean","COPY",FACE,{"derivedFrom":makeQuery(id+"F9.opExtrude","CAP_FACE",FACE,{"disambiguationData":[OSD([sQuery(id+"F8.wireOp",EDGE,"E13.0"),sQuery(id+"F8.wireOp",EDGE,"E13.1"),sQuery(id+"F8.wireOp",EDGE,"E14"),sQuery(id+"F8.wireOp",EDGE,"E15"),sQuery(id+"F8.wireOp",EDGE,"E16"),sQuery(id+"F8.wireOp",EDGE,"E18")])],"isStart":false})}),makeQuery(id+"F28.opExtrude","SWEPT_FACE",FACE,{"disambiguationData":[OSD([sQuery(id+"F27.wireOp",EDGE,"E43.right")])]}),makeQuery(id+"F28.opExtrude","SWEPT_FACE",FACE,{"disambiguationData":[OSD([sQuery(id+"F27.wireOp",EDGE,"E45.left")])]}),makeQuery(id+"F28.opExtrude","SWEPT_FACE",FACE,{"disambiguationData":[OSD([sQuery(id+"F27.wireOp",EDGE,"E47.right")])]}),makeQuery(id+"F28.opExtrude","SWEPT_FACE",FACE,{"disambiguationData":[OSD([sQuery(id+"F27.wireOp",EDGE,"E49.right")])]})]});
            var sketch = newSketch(context, id + "F32", { "sketchPlane" : qUnion([Q0])});
            skCircle(sketch, "E60", {"center": v(-54.6, -1.27) * mm, "radius": 2.9 * mm});
            skCircle(sketch, "E61", {"center": v(4.45, -1.27) * mm, "radius": 2.9 * mm});
            skCircle(sketch, "E62", {"center": v(63.5, -1.27) * mm, "radius": 2.9 * mm});
            skCircle(sketch, "E63", {"center": v(-85.46, -26.67) * mm, "radius": 2.9 * mm});
            skSolve(sketch);
        }
        {
            var Q0;
            Q0 = qSketchRegion(id + "F32", true);
            extrude(context, id + "F33", {"entities" : qUnion([Q0]), "operationType" : NewBodyOperationType.REMOVE, "oppositeDirection" : true, "depth" : 8.9 * mm});
        }
        {
            var Q0;
            Q0=makeQuery(id+"F28.boolean.opBoolean","MERGE",FACE,{"derivedFrom":[makeQuery(id+"F13.boolean.opBoolean","COPY",FACE,{"derivedFrom":makeQuery(id+"F13.opExtrude","CAP_FACE",FACE,{"disambiguationData":[OSD([sQuery(id+"F12.wireOp",EDGE,"E20"),sQuery(id+"F12.wireOp",EDGE,"E21"),sQuery(id+"F12.wireOp",EDGE,"E23"),sQuery(id+"F12.wireOp",EDGE,"E24"),sQuery(id+"F12.wireOp",EDGE,"E25"),sQuery(id+"F12.wireOp",EDGE,"E26")])],"isStart":false})}),makeQuery(id+"F28.opExtrude","SWEPT_FACE",FACE,{"disambiguationData":[OSD([sQuery(id+"F27.wireOp",EDGE,"E42.right")])]}),makeQuery(id+"F28.opExtrude","SWEPT_FACE",FACE,{"disambiguationData":[OSD([sQuery(id+"F27.wireOp",EDGE,"E44.left")])]}),makeQuery(id+"F28.opExtrude","SWEPT_FACE",FACE,{"disambiguationData":[OSD([sQuery(id+"F27.wireOp",EDGE,"E46.left")])]}),makeQuery(id+"F28.opExtrude","SWEPT_FACE",FACE,{"disambiguationData":[OSD([sQuery(id+"F27.wireOp",EDGE,"E48.left")])]})]});
            var sketch = newSketch(context, id + "F34", { "sketchPlane" : qUnion([Q0])});
            skCircle(sketch, "E64", {"center": v(-63.5, -1.27) * mm, "radius": 2.9 * mm});
            skCircle(sketch, "E65", {"center": v(-4.45, -1.27) * mm, "radius": 2.9 * mm});
            skCircle(sketch, "E66", {"center": v(54.61, -1.27) * mm, "radius": 2.9 * mm});
            skCircle(sketch, "E67", {"center": v(85.46, -26.67) * mm, "radius": 2.9 * mm});
            skSolve(sketch);
        }
        {
            var Q0;
            Q0 = qSketchRegion(id + "F34", true);
            extrude(context, id + "F35", {"entities" : qUnion([Q0]), "operationType" : NewBodyOperationType.REMOVE, "oppositeDirection" : true, "depth" : 8.9 * mm});
        }
        {
            var Q0;
            Q0=makeQuery(id+"F28.boolean.opBoolean","MERGE",FACE,{"derivedFrom":[makeQuery(id+"F11.boolean.opBoolean","COPY",FACE,{"derivedFrom":makeQuery(id+"F11.opExtrude","CAP_FACE",FACE,{"disambiguationData":[OSD([sQuery(id+"F10.wireOp",EDGE,"E19.bottom"),sQuery(id+"F10.wireOp",EDGE,"E19.top"),sQuery(id+"F10.wireOp",EDGE,"E19.left"),sQuery(id+"F10.wireOp",EDGE,"E19.right")])],"isStart":false})}),makeQuery(id+"F28.opExtrude","SWEPT_FACE",FACE,{"disambiguationData":[OSD([sQuery(id+"F27.wireOp",EDGE,"E46.bottom")])]}),makeQuery(id+"F28.opExtrude","SWEPT_FACE",FACE,{"disambiguationData":[OSD([sQuery(id+"F27.wireOp",EDGE,"E47.bottom")])]}),makeQuery(id+"F28.opExtrude","SWEPT_FACE",FACE,{"disambiguationData":[OSD([sQuery(id+"F27.wireOp",EDGE,"E50.top")])]})]});
            var sketch = newSketch(context, id + "F36", { "sketchPlane" : qUnion([Q0])});
            skCircle(sketch, "E68", {"center": v(0, -1.27) * mm, "radius": 2.9 * mm});
            skSolve(sketch);
        }
        {
            var Q0;
            Q0 = qSketchRegion(id + "F36", true);
            extrude(context, id + "F37", {"entities" : qUnion([Q0]), "operationType" : NewBodyOperationType.REMOVE, "oppositeDirection" : true, "depth" : 8.9 * mm});
        }
    });
